# Revit family: Normann_PLUS_PLS5A-R290
name_source: partatom
category: Attrezzature speciali
units: mm (PartAtom-declared; Revit-internal decimal feet)

## family parameters
Basato su piano di lavoro = No
Condiviso = No
Punto di calcolo locali = No
Quota connettore circolare = Usa diametro
Sempre verticale = Sì
Taglio con vuoti quando caricato = No
Tipo di parte = Normale

## types (16) — shared parameters
Asset Identifier = PLS5A-R290
Capacity internal - L = 115
Condensation = AIR
Controller = TFT
Depth Actual = 865 mm  [stored 2.83793 ft]
Depth Body = 795 mm  [stored 2.60827 ft]
Door Side R_L = No
Door_DX = No
Door_SX = Sì
GWP = 3
Gross Weight kg = 139
H_Feet_Limits = 117 mm
Height Actual = 954 mm  [stored 3.12992 ft]
Height_Door = 464 mm  [stored 1.52231 ft]
Height_Feet_100to160 = 117 mm
Ice cream pan 5l quantity (360x165x120mm) = 6
Internal depth actual - mm = 433 mm  [stored 1.4206 ft]
Internal height actual - mm = 410 mm  [stored 1.34514 ft]
Internal length actual - mm = 650 mm  [stored 2.13255 ft]
Length Actual = 750 mm  [stored 2.46063 ft]
Manufacturer = Normann
Mat_Frame = Acciaio inox, spazzolato
Mat_Grid = Acciaio inox, spazzolato
Max current cold cycle - A = 5.1
Max power cold cycle - W = 1203
Model Category = Blast chiller reach-in
Model Series = Plus
Net Weight kg = 124
OffSet_Display = 175 mm  [stored 0.574147 ft]
Packaging depth actual - mm = 890 mm  [stored 2.91995 ft]
Packaging height actual - mm = 1124 mm  [stored 3.68766 ft]
Packaging length actual - mm = 800 mm  [stored 2.62467 ft]
Packing volume - m3 = 0.8
Power Supply (Volts/Ph/Hz) = 220-240/1N/50
Refrigerant gas = R290
Refrigeration Climate Class = 4
Temperature range - °C = -40/+85
Tray Type = GN1/1 e EN1
Tray number = 5
URL Manufacturer = https://www.normann.it
Yield per blast chiling cycle (+90°C/+3°C) - kg = 23
Yield per blast chiling cycle +65/+10°C (EN22042) - kg = 18
Yield per blast chiling cycle consumption (EN22042) - kWh = 1
Yield per blast chiling cycle energy consumed (EN22042) - kWh/kg = 0.091
Yield per blast chiling cycle test time (EN22042) - min = 96
Yield per shock freezing cycle (+90/-18°C) - kg = 18
Yield per shock freezing cycle +65/-18°C (EN22042) - kg = 13
Yield per shock freezing cycle consuption (EN22042) - kWh = 4
Yield per shock freezing cycle energy consumed (EN22042) - kWh/kg = 0.322
Yield per shock freezing cycle test time (EN22042) - min = 261
zero-valued in all types: Liquid line diameter - mm, Prospetto di default, Suction line diameter - mm, Tray quantity EN1-GN1/1 h20mm, Tray quantity EN1-GN1/1 h40mm, Tray quantity EN1-GN1/1 h65mm, Tray quantity GN2/3 h65mm

## per-type parameters (varying)
| type | Feet | Height_Feet_Actual | ID | Max current warm cycle - A | Max power warm cycle - W | Optional | Wheel | Wheel_Feet |
| PLUS5 AIR, R290, 220-240/1N/50, TFT, LHH, FEET, MULTI POINT FOOD PROBE | Sì | 117 mm | 5A1C3D3B1-05B1B | 5.8 | 1350 | Multi point food probe | No | No |
| PLUS5 AIR, R290, 220-240/1N/50, TFT, LHH, WHEELS, MULTI POINT FOOD PROBE | No | 150 mm  [stored 0.492126 ft] | 5A1C3D3B1-05B1C | 5.8 | 1350 | Multi point food probe | Sì | Sì |
| PLUS5 AIR, R290, 220-240/1N/50, TFT, RHH, FEET, MULTI POINT FOOD PROBE | Sì | 117 mm | 5A1C3D3B1-05B2B | 5.8 | 1350 | Multi point food probe | No | No |
| PLUS5 AIR, R290, 220-240/1N/50, TFT, RHH, WHEELS, MULTI POINT FOOD PROBE | No | 150 mm  [stored 0.492126 ft] | 5A1C3D3B1-05B2C | 5.8 | 1350 | Multi point food probe | Sì | Sì |
| PLUS5 AIR, R290, 220-240/1N/50, TFT, LHH, FEET, MULTI FOOD PROBE | Sì | 117 mm | 5A1C3D3B1-05C1B | 5.8 | 1350 | Multi food probe | No | No |
| PLUS5 AIR, R290, 220-240/1N/50, TFT, LHH, WHEELS, MULTI FOOD PROBE | No | 150 mm  [stored 0.492126 ft] | 5A1C3D3B1-05C1C | 5.8 | 1350 | Multi food probe | Sì | Sì |
| PLUS5 AIR, R290, 220-240/1N/50, TFT, RHH, FEET, MULTI FOOD PROBE | Sì | 117 mm | 5A1C3D3B1-05C2B | 5.8 | 1350 | Multi food probe | No | No |
| PLUS5 AIR, R290, 220-240/1N/50, TFT, RHH, WHEELS, MULTI FOOD PROBE | No | 150 mm  [stored 0.492126 ft] | 5A1C3D3B1-05C2C | 5.8 | 1350 | Multi food probe | Sì | Sì |
| PLUS5 AIR, R290, 220-240/1N/50, TFT, LHH, FEET, MULTI POINT FOOD PROBE, WITH HUMIDITY CONTROL | Sì | 117 mm | 5A1C3D3B1-05E1B | 7.7 | 1750 | Multi point food probe - with humidity control | No | No |
| PLUS5 AIR, R290, 220-240/1N/50, TFT, LHH, WHEELS, MULTI POINT FOOD PROBE, WITH HUMIDITY CONTROL | No | 150 mm  [stored 0.492126 ft] | 5A1C3D3B1-05E1C | 7.7 | 1750 | Multi point food probe - with humidity control | Sì | Sì |
| PLUS5 AIR, R290, 220-240/1N/50, TFT, RHH, FEET, MULTI POINT FOOD PROBE, WITH HUMIDITY CONTROL | Sì | 117 mm | 5A1C3D3B1-05E2B | 7.7 | 1750 | Multi point food probe - with humidity control | No | No |
| PLUS5 AIR, R290, 220-240/1N/50, TFT, RHH, WHEELS, MULTI POINT FOOD PROBE, WITH HUMIDITY CONTROL | No | 150 mm  [stored 0.492126 ft] | 5A1C3D3B1-05E2C | 7.7 | 1750 | Multi point food probe - with humidity control | Sì | Sì |
| PLUS5 AIR, R290, 220-240/1N/50, TFT, LHH, FEET, MULTI FOOD PROBE, WITH HUMIDITY CONTROL | Sì | 117 mm | 5A1C3D3B1-05F1B | 7.7 | 1750 | Multi food probe - with humidity control | No | No |
| PLUS5 AIR, R290, 220-240/1N/50, TFT, LHH, WHEELS, MULTI FOOD PROBE, WITH HUMIDITY CONTROL | No | 150 mm  [stored 0.492126 ft] | 5A1C3D3B1-05F1C | 7.7 | 1750 | Multi food probe - with humidity control | Sì | Sì |
| PLUS5 AIR, R290, 220-240/1N/50, TFT, RHH, FEET, MULTI FOOD PROBE, WITH HUMIDITY CONTROL | Sì | 117 mm | 5A1C3D3B1-05F2B | 7.7 | 1750 | Multi food probe - with humidity control | No | No |
| PLUS5 AIR, R290, 220-240/1N/50, TFT, RHH, WHEELS, MULTI FOOD PROBE, WITH HUMIDITY CONTROL | No | 150 mm  [stored 0.492126 ft] | 5A1C3D3B1-05F2C | 7.7 | 1750 | Multi food probe - with humidity control | Sì | Sì |

note: [stored X ft] marks values corroborated as IEEE doubles in the binary element streams (Revit-internal decimal feet)
